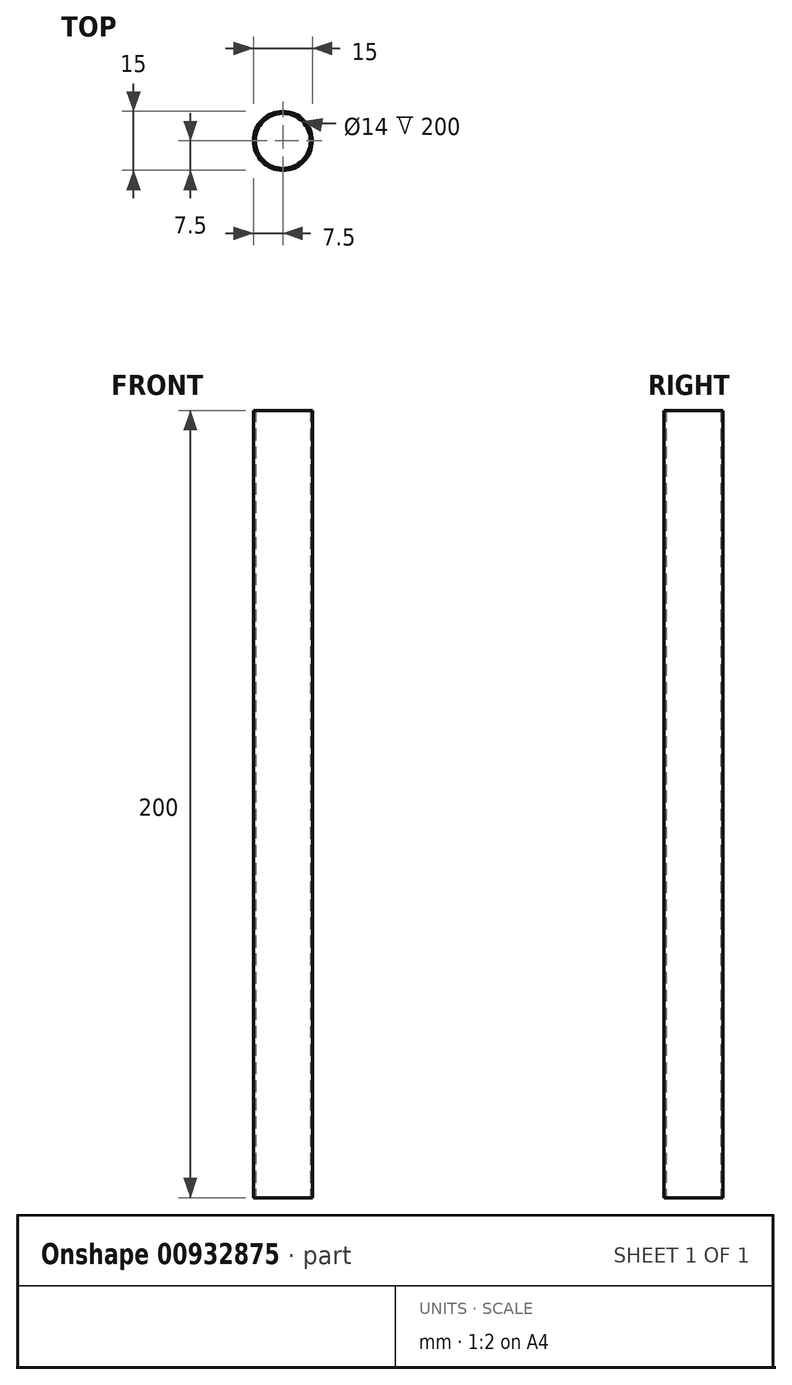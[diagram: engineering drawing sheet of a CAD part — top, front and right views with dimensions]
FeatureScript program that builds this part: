
annotation { "Feature Type Name" : "Feature", "Feature Type Description" : "" }
export const myFeature = defineFeature(function(context is Context, id is Id, definition is map)
    precondition{}
    {
        {
            var Q0;
            Q0=qCreatedBy(makeId("Top.planeOp"),FACE);
            var sketch = newSketch(context, id + "F0", { "sketchPlane" : qUnion([Q0])});
            skCircle(sketch, "E0", {"center": v(0, 0) * mm, "radius": 7.5 * mm});
            skCircle(sketch, "E1", {"center": v(0, 0) * mm, "radius": 7 * mm});
            skSolve(sketch);
        }
        {
            var Q0;
            Q0=makeQuery(id+"F0.imprint","IMPRINT",FACE,{"disambiguationData":[TD([[makeQuery(id+"F0.imprint","IMPRINT",EDGE,{"derivedFrom":sQuery(id+"F0.wireOp",EDGE,"E0")}),1.0]])]});
            extrude(context, id + "F1", {"entities" : qUnion([Q0]), "depth" : 200 * mm, "offsetDistance" : 25 * mm});
        }
    });
